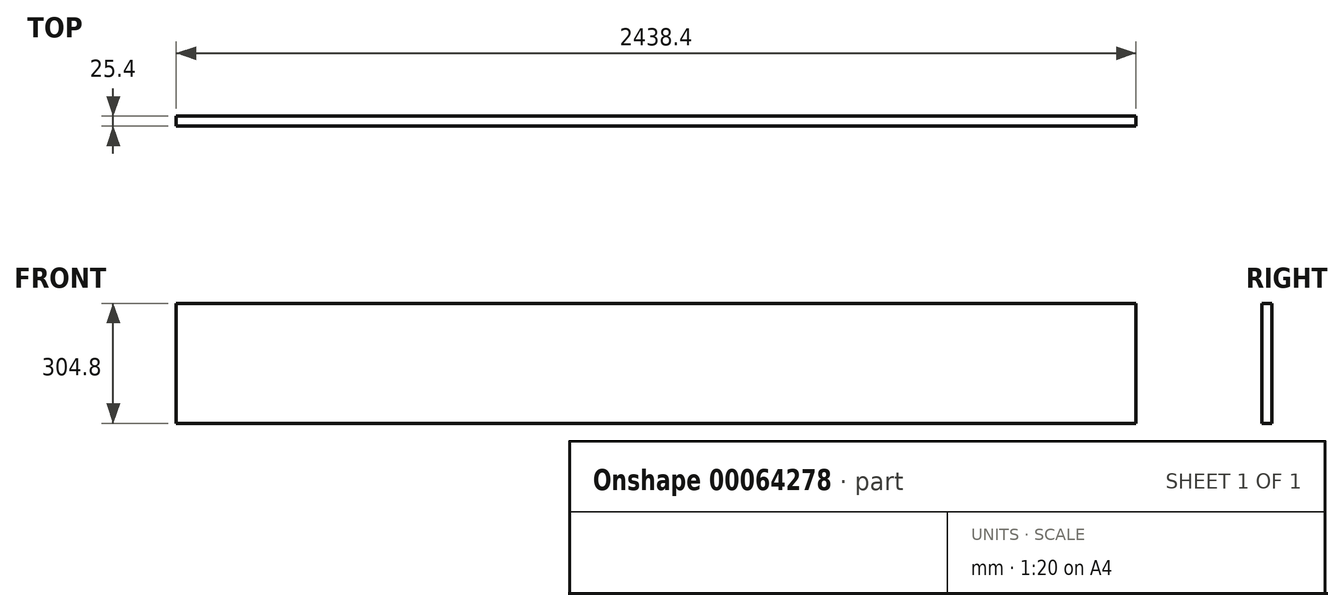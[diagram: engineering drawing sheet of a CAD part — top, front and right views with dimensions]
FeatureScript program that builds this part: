
annotation { "Feature Type Name" : "Feature", "Feature Type Description" : "" }
export const myFeature = defineFeature(function(context is Context, id is Id, definition is map)
    precondition{}
    {
        {
            var Q0;
            Q0=qCreatedBy(makeId("Front.planeOp"),FACE);
            var sketch = newSketch(context, id + "F0", { "sketchPlane" : qUnion([Q0])});
            skLineSegment(sketch, "E0.bottom", {"start": v(-1219.2, 152.4) * mm, "end": v(1219.2, 152.4) * mm});
            skLineSegment(sketch, "E0.top", {"start": v(-1219.2, -152.4) * mm, "end": v(1219.2, -152.4) * mm});
            skLineSegment(sketch, "E0.left", {"start": v(-1219.2, 152.4) * mm, "end": v(-1219.2, -152.4) * mm});
            skLineSegment(sketch, "E0.right", {"start": v(1219.2, 152.4) * mm, "end": v(1219.2, -152.4) * mm});
            skLineSegment(sketch, "E1", {"start": v(-1219.2, 0) * mm, "end": v(0, 0) * mm, "construction": true});
            skLineSegment(sketch, "E2", {"start": v(0, 152.4) * mm, "end": v(0, 0) * mm, "construction": true});
            skSolve(sketch);
        }
        {
            var Q0;
            Q0=makeQuery(id+"F0.imprint","IMPRINT",FACE,{"disambiguationData":[TD([[makeQuery(id+"F0.imprint","IMPRINT",EDGE,{"derivedFrom":sQuery(id+"F0.wireOp",EDGE,"E0.bottom")}),-1.0]])]});
            extrude(context, id + "F1", {"entities" : qUnion([Q0]), "oppositeDirection" : true, "depth" : 25.4 * mm});
        }
    });
